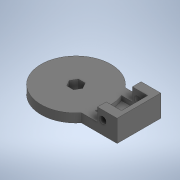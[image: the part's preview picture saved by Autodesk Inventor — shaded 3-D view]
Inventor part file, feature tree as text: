
AUTODESK INVENTOR PART (.ipt)
format: ipt  version: 2021.1 (Build 251245000, 245)  size: 201,216 bytes
history: native  units: in
note: dims shown in document units (in); Inventor stores cm internally (conversion verified against a paired STEP export)
features: extrude x7, sketch x7, other x2, revolve x1, mirror x1, reference x1
ambient origin geometry x8: Origin, YZ Plane, XZ Plane, XY Plane, X Axis, Y Axis, Z Axis, Center Point
bodies: Solid1 (feature_tree)
feature tree (19):
  revolve  "Revolution1"  [1 undecoded]
  extrude  "Extrusion1"  TaperAngle=90.0deg  [1 undecoded]
  extrude  "Extrusion3"  Depth=1.24in
  extrude  "Extrusion4"  Depth=0.5in TaperAngle=0.0deg
  extrude  "Extrusion5"  Depth=0.5in
  mirror  "Mirror1"
  extrude  "Extrusion6"  Depth=0.5in TaperAngle=0.0deg
  extrude  "Extrusion7"  Depth=0.75in TaperAngle=0.0deg
  extrude  "Extrusion8"  Depth=1.5in
  sketch  "Sketch5"  dims[d0=2.0in d1=0.1969in]
  sketch  "Sketch7"  dims[d2=0.4751in d6=90.0deg]
  sketch  "Sketch8"  dims[d13=1.4in d15=1.24in]
  sketch  "Sketch9"  dims[d16=0.6693in d17=0.5in d18=0.0in]
  reference  "Reference1"
  sketch  "Sketch10"  dims[d23=1.5in d24=0.5in]
  sketch  "Sketch11"  dims[d25=0.75in d26=0.5in d27=0.0in]
  sketch  "Sketch13"  dims[d28=0.875in d29=0.75in d30=0.0in d31=0.39in d32=0.0in d33=0.0in d34=0.25in d35=0.0in d36=0.25in d37=0.0in d38=0.5in d39=1.5in d40=0.0in d41=0.0in]
  other  "ForkMountWithCelestronTubeConnector.iam"
  other  "6x3_8-keyedDriveShaft:2"
note: 2 required parameter values undecoded (feature->parameter linkage not recoverable at this tier; creation-order binding heuristic only, values carry confidence <= 0.55)